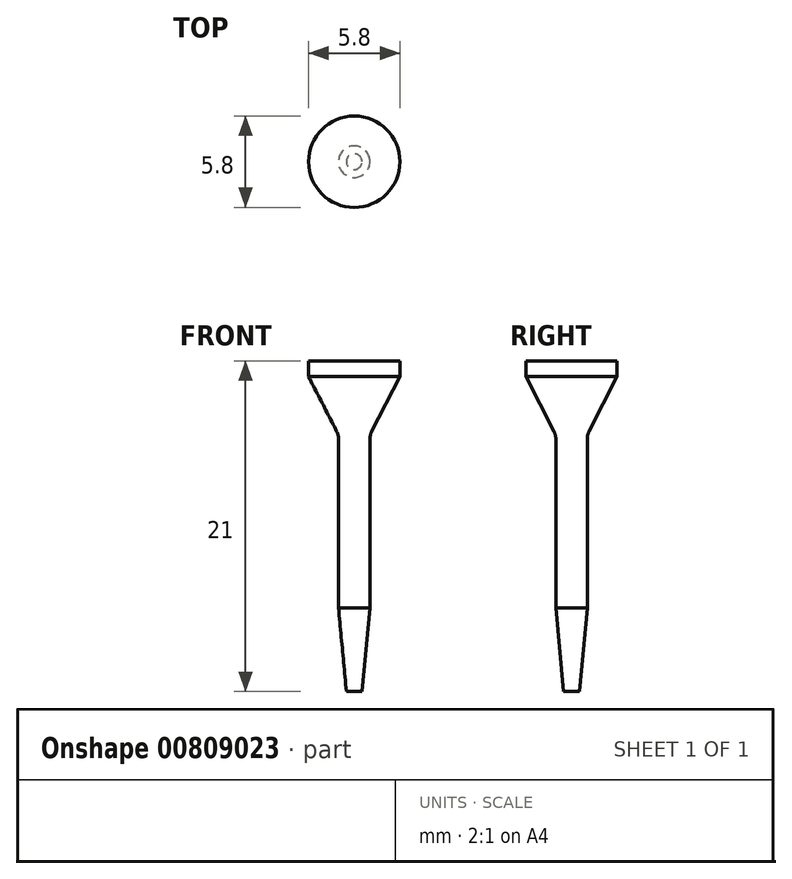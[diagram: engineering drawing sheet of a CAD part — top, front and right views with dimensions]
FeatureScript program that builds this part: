
annotation { "Feature Type Name" : "Feature", "Feature Type Description" : "" }
export const myFeature = defineFeature(function(context is Context, id is Id, definition is map)
    precondition{}
    {
        {
            var Q0;
            Q0=qCreatedBy(makeId("Front.planeOp"),FACE);
            var sketch = newSketch(context, id + "F0", { "sketchPlane" : qUnion([Q0])});
            skLineSegment(sketch, "E0", {"start": v(0, 0) * mm, "end": v(0.5, 0) * mm});
            skLineSegment(sketch, "E1", {"start": v(0.5, 0) * mm, "end": v(1, 5.3) * mm});
            skLineSegment(sketch, "E2", {"start": v(1, 5.3) * mm, "end": v(1, 16.06) * mm});
            skLineSegment(sketch, "E3", {"start": v(1.11, 16.52) * mm, "end": v(2.9, 20) * mm});
            skLineSegment(sketch, "E4", {"start": v(2.9, 21) * mm, "end": v(0, 21) * mm});
            skLineSegment(sketch, "E5", {"start": v(0, 0) * mm, "end": v(0, 21) * mm});
            skPoint(sketch, "E6.visualSharp", {"position": v(1, 17.3) * mm});
            skArc(sketch, "E6.filletArc", {"start": v(1.11, 16.52) * mm, "mid": v(1.03, 16.3) * mm, "end": v(1, 16.06) * mm});
            skLineSegment(sketch, "E7", {"start": v(2.9, 21) * mm, "end": v(2.9, 20) * mm});
            skSolve(sketch);
        }
        {
            var Q0;
            Q0=makeQuery(id+"F0.imprint","IMPRINT",FACE,{"disambiguationData":[TD([[makeQuery(id+"F0.imprint","IMPRINT",EDGE,{"derivedFrom":sQuery(id+"F0.wireOp",EDGE,"E0")}),1.0]])]});
            var Q1;
            Q1=sQuery(id+"F0.wireOp",EDGE,"E5");
            revolve(context, id + "F1", {"surfaceOperationType" : NewSurfaceOperationType.NEW, "entities" : qUnion([Q0]), "axis" : qUnion([Q1]), "revolveType" : RevolveType.FULL});
        }
    });
